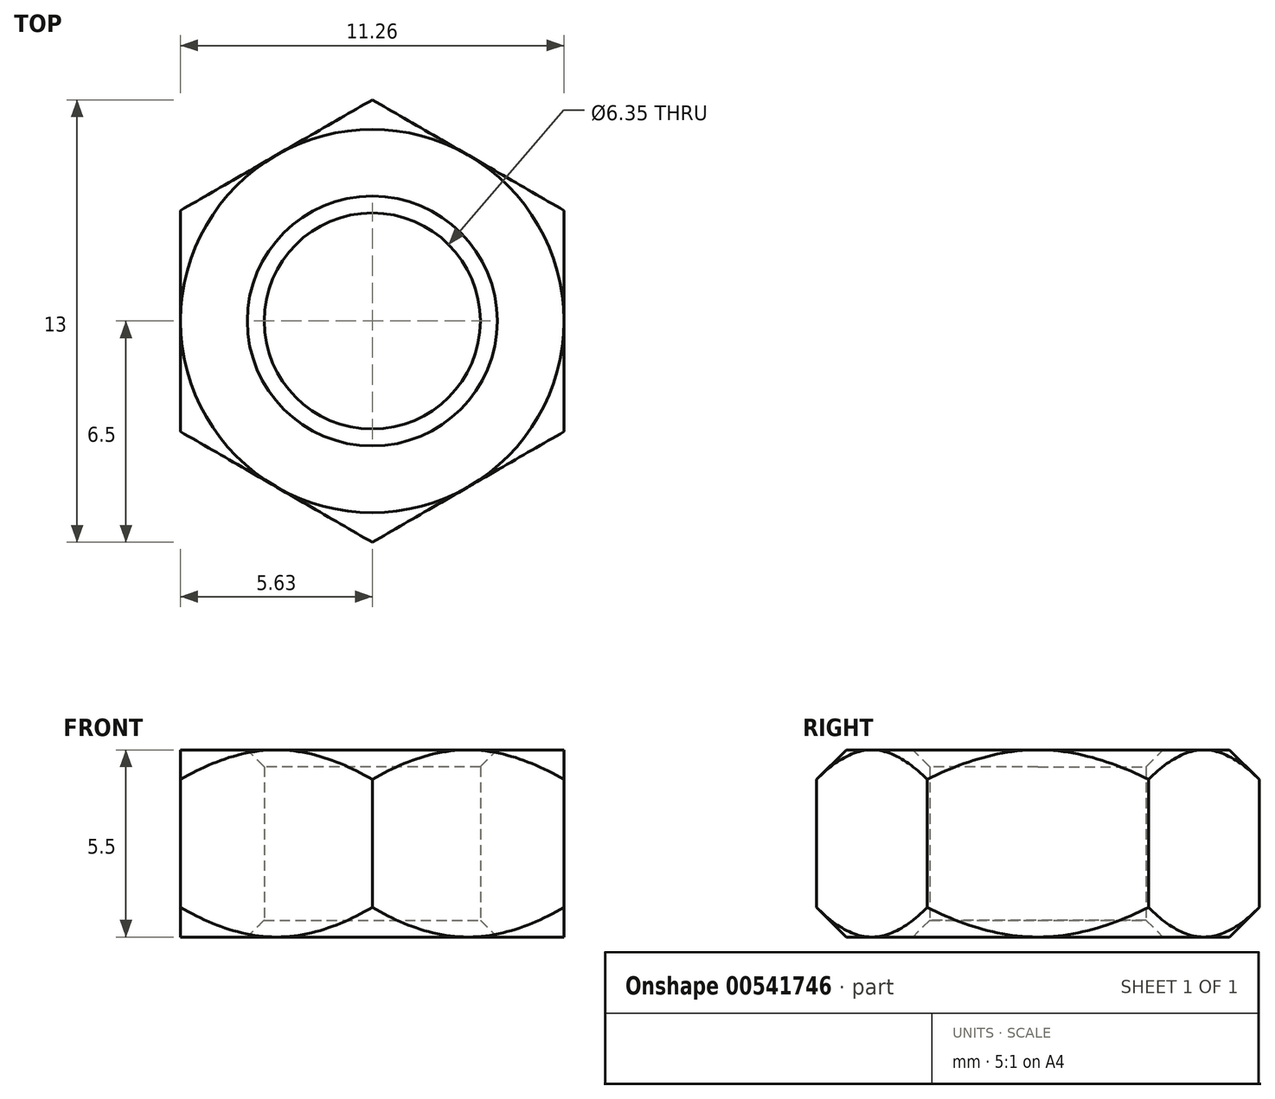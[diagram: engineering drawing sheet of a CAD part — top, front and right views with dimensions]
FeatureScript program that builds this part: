
annotation { "Feature Type Name" : "Feature", "Feature Type Description" : "" }
export const myFeature = defineFeature(function(context is Context, id is Id, definition is map)
    precondition{}
    {
        {
            var Q0;
            Q0=qCreatedBy(makeId("Top.planeOp"),FACE);
            var sketch = newSketch(context, id + "F0", { "sketchPlane" : qUnion([Q0])});
            skLineSegment(sketch, "E0", {"start": v(0, 60) * mm, "end": v(0, -60) * mm});
            skLineSegment(sketch, "E1", {"start": v(-70, 0) * mm, "end": v(70, 0) * mm});
            skCircle(sketch, "E2", {"center": v(0, 0) * mm, "radius": 3.17 * mm});
            skLineSegment(sketch, "E3", {"start": v(0, 6.5) * mm, "end": v(5.63, 3.25) * mm});
            skLineSegment(sketch, "E4", {"start": v(5.63, 3.25) * mm, "end": v(5.63, -3.25) * mm});
            skLineSegment(sketch, "E5", {"start": v(5.63, -3.25) * mm, "end": v(0, -6.5) * mm});
            skLineSegment(sketch, "E6", {"start": v(0, 6.5) * mm, "end": v(-5.63, 3.25) * mm});
            skLineSegment(sketch, "E7", {"start": v(-5.63, 3.25) * mm, "end": v(-5.63, -3.25) * mm});
            skLineSegment(sketch, "E8", {"start": v(-5.63, -3.25) * mm, "end": v(0, -6.5) * mm});
            skSolve(sketch);
        }
        {
            var Q0;
            {var subQ0=sQuery(id+"F0.wireOp",EDGE,"E6");Q0=makeQuery(id+"F0.imprint","IMPRINT",FACE,{"disambiguationData":[TD([[makeQuery(id+"F0.imprint","IMPRINT",EDGE,{"derivedFrom":subQ0}),1.0]])]});}
            var Q1;
            {var subQ7=sQuery(id+"F0.wireOp",EDGE,"E8");Q1=makeQuery(id+"F0.imprint","IMPRINT",FACE,{"disambiguationData":[TD([[makeQuery(id+"F0.imprint","IMPRINT",EDGE,{"derivedFrom":subQ7}),1.0]])]});}
            var Q2;
            {var subQ0=sQuery(id+"F0.wireOp",EDGE,"E5");Q2=makeQuery(id+"F0.imprint","IMPRINT",FACE,{"disambiguationData":[TD([[makeQuery(id+"F0.imprint","IMPRINT",EDGE,{"derivedFrom":subQ0}),-1.0]])]});}
            var Q3;
            {var subQ5=sQuery(id+"F0.wireOp",EDGE,"E3");Q3=makeQuery(id+"F0.imprint","IMPRINT",FACE,{"disambiguationData":[TD([[makeQuery(id+"F0.imprint","IMPRINT",EDGE,{"derivedFrom":subQ5}),-1.0]])]});}
            extrude(context, id + "F1", {"entities" : qUnion([Q0, Q1, Q2, Q3]), "depth" : 5.5 * mm, "offsetDistance" : 25 * mm});
        }
        {
            var Q0;
            Q0=qCreatedBy(makeId("Front.planeOp"),FACE);
            var sketch = newSketch(context, id + "F2", { "sketchPlane" : qUnion([Q0])});
            skLineSegment(sketch, "E9", {"start": v(0, 60) * mm, "end": v(0, -60) * mm});
            skLineSegment(sketch, "E10", {"start": v(-70, 0) * mm, "end": v(70, 0) * mm});
            skLineSegment(sketch, "E11", {"start": v(3.17, 0.5) * mm, "end": v(3.17, 5) * mm});
            skLineSegment(sketch, "E12", {"start": v(3.67, 5.5) * mm, "end": v(5.63, 5.5) * mm});
            skLineSegment(sketch, "E13", {"start": v(3.67, 0) * mm, "end": v(5.63, 0) * mm});
            skLineSegment(sketch, "E14", {"start": v(3.17, 5) * mm, "end": v(3.67, 5.5) * mm});
            skLineSegment(sketch, "E15", {"start": v(3.17, 0.5) * mm, "end": v(3.67, 0) * mm});
            skLineSegment(sketch, "E16", {"start": v(7.12, 1.5) * mm, "end": v(5.63, 0) * mm});
            skLineSegment(sketch, "E17", {"start": v(7.12, 4) * mm, "end": v(5.63, 5.5) * mm});
            skLineSegment(sketch, "E18", {"start": v(7.12, 4) * mm, "end": v(7.12, 1.5) * mm});
            skSolve(sketch);
        }
        {
            var Q0;
            Q0 = qSketchRegion(id + "F2", true);
            var Q1;
            Q1=makeQuery(id+"F2.imprint","IMPRINT",FACE,{"disambiguationData":[TD([[makeQuery(id+"F2.imprint","IMPRINT",EDGE,{"derivedFrom":sQuery(id+"F2.wireOp",EDGE,"E11")}),-1.0]])]});
            var Q2;
            Q2=sQuery(id+"F2.wireOp",EDGE,"E9");
            revolve(context, id + "F3", {"entities" : qUnion([Q0, Q1]), "axis" : qUnion([Q2]), "revolveType" : RevolveType.FULL});
        }
        {
            var Q0;
            Q0=makeQuery(id+"F1.opExtrude","SWEPT_BODY",BODY,{"disambiguationData":[OSD([sQuery(id+"F0.wireOp",EDGE,"E2"),sQuery(id+"F0.wireOp",EDGE,"E3"),sQuery(id+"F0.wireOp",EDGE,"E4"),sQuery(id+"F0.wireOp",EDGE,"E5"),sQuery(id+"F0.wireOp",EDGE,"E6"),sQuery(id+"F0.wireOp",EDGE,"E7"),sQuery(id+"F0.wireOp",EDGE,"E8")])]});
            var Q1;
            Q1=makeQuery(id+"F3.opRevolve","SWEPT_BODY",BODY,{"disambiguationData":[OSD([sQuery(id+"F2.wireOp",EDGE,"E11"),sQuery(id+"F2.wireOp",EDGE,"E12"),sQuery(id+"F2.wireOp",EDGE,"E13"),sQuery(id+"F2.wireOp",EDGE,"E14"),sQuery(id+"F2.wireOp",EDGE,"E15"),sQuery(id+"F2.wireOp",EDGE,"E16"),sQuery(id+"F2.wireOp",EDGE,"E17"),sQuery(id+"F2.wireOp",EDGE,"E18")])]});
            booleanBodies(context, id + "F4", {"operationType" : BooleanOperationType.INTERSECTION, "tools" : qUnion([Q0, Q1])});
        }
    });
